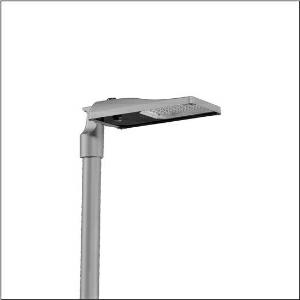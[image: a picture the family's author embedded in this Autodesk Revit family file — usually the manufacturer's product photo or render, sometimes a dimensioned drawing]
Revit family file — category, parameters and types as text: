
# Revit family: streetlight_sl_31_mini___p0_5a_5xh6v31t08ja_e515
name_source: partatom
category: Lighting Fixtures
units: mm (PartAtom-declared; Revit-internal decimal feet)

## family parameters
Cut with Voids When Loaded = No
Host = Face
Light Source = No
Part Type = Normal
Room Calculation Point = No
Round Connector Dimension = Use Diameter
Shared = No

## types (1)
- --- (1 x LED, 12050 lm, 82.5 W, 3000K)
    Apparent Load = 83 VA
    CIE Flux Codes = 37 73 96 100 100
    Color Rendering = 70
    Color Temperature = 3000K
    Default Elevation = 1800 mm
    Description = Streetlight SL 31 mini D4i, Desk-Remote mast luminaire for post-top, side-entry; light control with lens of PMMA; light distribution: P0.5a, direct asymmetric distribution, for standard-compliant lighting for roads and squares; LED: luminous flux: 12.050lm, light colour: 730, colour temperature: 3000K; luminous efficacy: 146,1lm/W; control: pre-setting: logarithmic dimming characteristic, flexible luminous flux parameterisation, time-dependent luminous flux control, constant luminous flux control, power reduction, intelligent temperature release in ECG and LED module, overheat protection; luminaire housing, of diecast aluminium, Siteco® metallic grey (DB 702S), corrosivity category C5 high according to DIN EN ISO 12944; cover of toughened safety glass, transparent, opened without tools; mast flange of diecast aluminium, Siteco® metallic grey (DB 702S), spigot size: 76/60mm, mast flange included unmounted; with cable H07RN-F 2x 1.5mm², cable length: 10,5m, connection cable pre-assembled; mains connection: 220..240V, AC, 50/60Hz; power consumption (at start of service life): 82,5W / (at end of service life): 90,1W / (with reduced operation 50%): 36,8W; protection rating (complete): IP66; insulation class (complete): insulation class II (safety insulation); impact resistance: IK09; certification: CE, ENEC, ENEC+, VDE, UKCA, ZD4i; permissible operating ambient temperature for outdoor applications: -40..+50°C; packaging unit: 1 piece

Light Distribution: P0.5a
    Height = 76 mm
    Lamp = 1 x LED
    Lamp Light Flux = 12050 lm
    Lamp Power = 82.5 W
    Lamp count = 1
    Length = 547 mm
    Luminous efficacy = 146 lm/W
    Manufacturer = Siteco
    ModVariant = No
    Model = 5XH6V31T08JA
    Number of Poles = 1
    OnlyDefault = Yes
    Power Factor = 1
    Product Name = Streetlight SL 31 mini | P0.5a
    Product group = mast luminaire | pylon top
    ProductGroupID = 6100
    Protection Class = Protection class II
    Protection Degree = IP 66
    RLX_Detail_Level = 1
    RLX_Emergency_Light_Flux = 0 lm
    RLX_Emergency_Type = 0
    RLX_Emergency_Type_DB = No
    RlxData = <blob elided: 39677 chars, md5=551aacd6>
    Socket = socket
    Standby Power = 0 W
    System Light Flux = 12050 lm
    System Power = 83 W
    Type Comments = factory setting: luminous flux: 100 % | dim-lin: 254 | 870 mA
    Type Image = l_1300332.jpg
    URL = http://relux.com
    VarID = @adj_058478
    Voltage = 0 V
    Weight = 0.00 kg
    Width = 265 mm

## geometry (parser evidence)
native form markers: Blend x4, Sweep x8
no freeform markers — native parametric forms only
